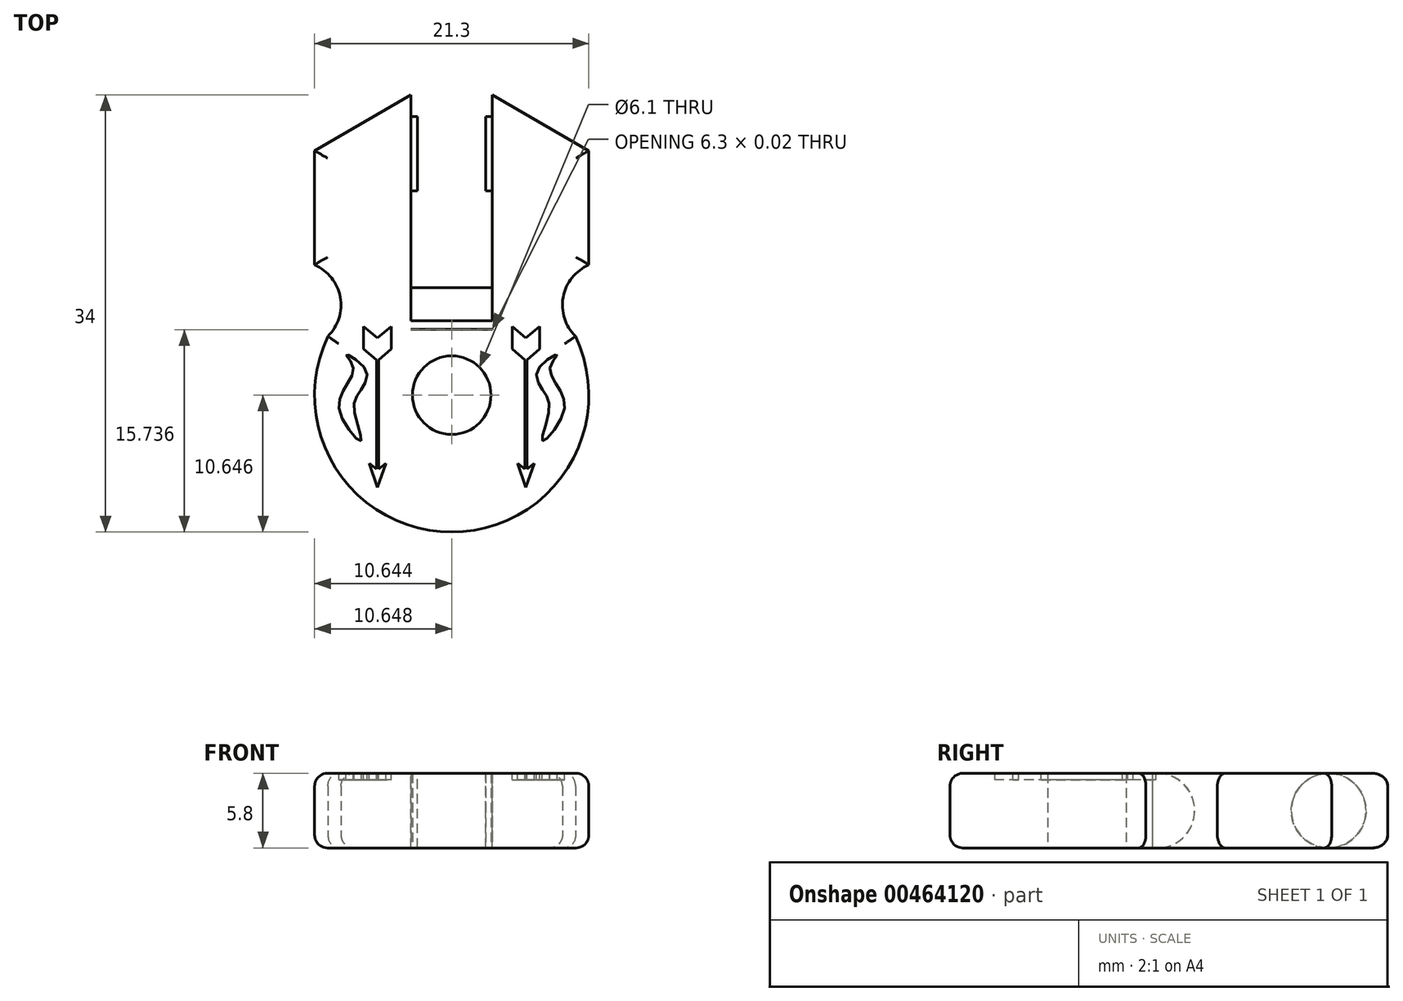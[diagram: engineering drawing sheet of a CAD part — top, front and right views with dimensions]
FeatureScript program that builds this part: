
annotation { "Feature Type Name" : "Feature", "Feature Type Description" : "" }
export const myFeature = defineFeature(function(context is Context, id is Id, definition is map)
    precondition{}
    {
        {
            var Q0;
            Q0=qCreatedBy(makeId("Top.planeOp"),FACE);
            var sketch = newSketch(context, id + "F0", { "sketchPlane" : qUnion([Q0])});
            skArc(sketch, "E0", {"start": v(-38.89, 15.42) * mm, "mid": v(-29.27, 0.2) * mm, "end": v(-19.65, 15.42) * mm});
            skLineSegment(sketch, "E1", {"start": v(-18.62, 29.85) * mm, "end": v(-26.13, 34.2) * mm});
            skLineSegment(sketch, "E2", {"start": v(-18.62, 29.85) * mm, "end": v(-18.62, 20.97) * mm});
            skPoint(sketch, "E3.start.orphan", {"position": v(-18.62, 10.85) * mm});
            skPoint(sketch, "E4.end.orphan", {"position": v(-18.32, 15.95) * mm});
            skLineSegment(sketch, "E5", {"start": v(-32.43, 34.2) * mm, "end": v(-39.92, 29.85) * mm});
            skLineSegment(sketch, "E6", {"start": v(-39.92, 29.85) * mm, "end": v(-39.92, 20.85) * mm});
            skPoint(sketch, "E7.end.orphan", {"position": v(-39.92, 34.2) * mm});
            skArc(sketch, "E8", {"start": v(-38.89, 15.42) * mm, "mid": v(-37.93, 18.47) * mm, "end": v(-39.92, 20.97) * mm});
            skPoint(sketch, "E9.orphan", {"position": v(-38.4, 16.32) * mm});
            skPoint(sketch, "E10.end.orphan", {"position": v(-29.27, -3.17) * mm});
            skArc(sketch, "E11", {"start": v(-18.62, 20.97) * mm, "mid": v(-20.61, 18.47) * mm, "end": v(-19.65, 15.42) * mm});
            skPoint(sketch, "E12.orphan", {"position": v(-20.14, 16.32) * mm});
            skLineSegment(sketch, "E13", {"start": v(-32.43, 34.2) * mm, "end": v(-32.43, 15.95) * mm});
            skLineSegment(sketch, "E14", {"start": v(-26.13, 34.2) * mm, "end": v(-26.13, 15.93) * mm});
            skPoint(sketch, "E15.end.orphan", {"position": v(-26.12, 15.93) * mm});
            skPoint(sketch, "E16.start.orphan", {"position": v(-29.27, 15.95) * mm});
            skPoint(sketch, "E17.start.orphan", {"position": v(-32.42, 15.95) * mm});
            skLineSegment(sketch, "E18", {"start": v(-26.13, 15.93) * mm, "end": v(-32.43, 15.95) * mm});
            skPoint(sketch, "E19.start.orphan", {"position": v(-26.13, 34.2) * mm});
            skPoint(sketch, "E20.orphan", {"position": v(-32.43, 34.2) * mm});
            skCircle(sketch, "E21", {"center": v(-29.27, 10.85) * mm, "radius": 3.05 * mm});
            skSolve(sketch);
        }
        {
            var Q0;
            Q0=qSketchRegion(id+"F0",true);
            extrude(context, id + "F1", {"entities" : qUnion([Q0]), "depth" : 5.8 * mm});
        }
        {
            var Q0;
            Q0=makeQuery(id+"F1.opExtrude","CAP_EDGE",EDGE,{"disambiguationData":[OSD([sQuery(id+"F0.wireOp",EDGE,"E0")])],"isStart":false});
            var Q1;
            Q1=makeQuery(id+"F1.opExtrude","CAP_EDGE",EDGE,{"disambiguationData":[OSD([sQuery(id+"F0.wireOp",EDGE,"E11")])],"isStart":false});
            var Q2;
            Q2=makeQuery(id+"F1.opExtrude","CAP_EDGE",EDGE,{"disambiguationData":[OSD([sQuery(id+"F0.wireOp",EDGE,"E2")])],"isStart":false});
            var Q3;
            Q3=makeQuery(id+"F1.opExtrude","CAP_EDGE",EDGE,{"disambiguationData":[OSD([sQuery(id+"F0.wireOp",EDGE,"E8")])],"isStart":false});
            var Q4;
            Q4=makeQuery(id+"F1.opExtrude","CAP_EDGE",EDGE,{"disambiguationData":[OSD([sQuery(id+"F0.wireOp",EDGE,"E6")])],"isStart":false});
            var Q5;
            Q5=makeQuery(id+"F1.opExtrude","CAP_EDGE",EDGE,{"disambiguationData":[OSD([sQuery(id+"F0.wireOp",EDGE,"E5")])],"isStart":false});
            var Q6;
            Q6=makeQuery(id+"F1.opExtrude","CAP_EDGE",EDGE,{"disambiguationData":[OSD([sQuery(id+"F0.wireOp",EDGE,"E1")])],"isStart":false});
            var Q7;
            Q7=makeQuery(id+"F1.opExtrude","CAP_EDGE",EDGE,{"disambiguationData":[OSD([sQuery(id+"F0.wireOp",EDGE,"E0")])],"isStart":true});
            var Q8;
            Q8=makeQuery(id+"F1.opExtrude","CAP_EDGE",EDGE,{"disambiguationData":[OSD([sQuery(id+"F0.wireOp",EDGE,"E11")])],"isStart":true});
            var Q9;
            Q9=makeQuery(id+"F1.opExtrude","CAP_EDGE",EDGE,{"disambiguationData":[OSD([sQuery(id+"F0.wireOp",EDGE,"E8")])],"isStart":true});
            var Q10;
            Q10=makeQuery(id+"F1.opExtrude","CAP_EDGE",EDGE,{"disambiguationData":[OSD([sQuery(id+"F0.wireOp",EDGE,"E6")])],"isStart":true});
            var Q11;
            Q11=makeQuery(id+"F1.opExtrude","CAP_EDGE",EDGE,{"disambiguationData":[OSD([sQuery(id+"F0.wireOp",EDGE,"E2")])],"isStart":true});
            var Q12;
            Q12=makeQuery(id+"F1.opExtrude","CAP_EDGE",EDGE,{"disambiguationData":[OSD([sQuery(id+"F0.wireOp",EDGE,"E1")])],"isStart":true});
            var Q13;
            Q13=makeQuery(id+"F1.opExtrude","CAP_EDGE",EDGE,{"disambiguationData":[OSD([sQuery(id+"F0.wireOp",EDGE,"E5")])],"isStart":true});
            fillet(context, id + "F2", {"entities" : qUnion([Q0, Q1, Q2, Q3, Q4, Q5, Q6, Q7, Q8, Q9, Q10, Q11, Q12, Q13]), "radius" : 1 * mm, "tangentPropagation" : true, "allowEdgeOverflow" : false});
        }
        {
            var Q0;
            Q0=makeQuery(id+"F1.opExtrude","SWEPT_FACE",FACE,{"disambiguationData":[OSD([sQuery(id+"F0.wireOp",EDGE,"E13")])]});
            var sketch = newSketch(context, id + "F3", { "sketchPlane" : qUnion([Q0])});
            skCircle(sketch, "E22", {"center": v(29.6, 2.9) * mm, "radius": 2.9 * mm});
            skPoint(sketch, "E23.orphan", {"position": v(34.2, 2.9) * mm});
            skArc(sketch, "E24", {"start": v(15.95, 0) * mm, "mid": v(19.2, 2.9) * mm, "end": v(15.95, 5.8) * mm});
            skSolve(sketch);
        }
        {
            var Q0;
            {var subQ0=sQuery(id+"F3.wireOp",EDGE,"E22");var subQ1=sQuery(id+"F0.wireOp",EDGE,"E13");var subQ2=makeQuery(id+"F3.imprint","INTERSECT",VERTEX,{"derivedFrom":[makeQuery(id+"F1.opExtrude","CAP_EDGE",EDGE,{"disambiguationData":[OSD([subQ1])],"isStart":true}),subQ0]});Q0=makeQuery(id+"F3.imprint","IMPRINT",FACE,{"disambiguationData":[TD([[makeQuery(id+"F3.imprint","IMPRINT",EDGE,{"disambiguationData":[TD([[subQ2,1.0]])],"derivedFrom":subQ0}),1.0]])]});}
            extrude(context, id + "F4", {"entities" : qUnion([Q0]), "operationType" : NewBodyOperationType.ADD, "depth" : .5 * mm});
        }
        {
            var Q0;
            {var subQ1=sQuery(id+"F0.wireOp",EDGE,"E13");var subQ6=makeQuery(id+"F1.opExtrude","SWEPT_EDGE",EDGE,{"disambiguationData":[OSD([subQ1,sQuery(id+"F0.wireOp",EDGE,"E18")])]});Q0=makeQuery(id+"F3.imprint","IMPRINT",FACE,{"disambiguationData":[TD([[makeQuery(id+"F3.imprint","IMPRINT",EDGE,{"derivedFrom":subQ6}),1.0]])]});}
            extrude(context, id + "F5", {"entities" : qUnion([Q0]), "operationType" : NewBodyOperationType.ADD, "depth" : 8.2 * mm});
        }
        {
            var Q0;
            Q0=makeQuery(id+"F1.opExtrude","SWEPT_FACE",FACE,{"disambiguationData":[OSD([sQuery(id+"F0.wireOp",EDGE,"E14")])]});
            var sketch = newSketch(context, id + "F6", { "sketchPlane" : qUnion([Q0])});
            skCircle(sketch, "E25", {"center": v(-29.6, 2.9) * mm, "radius": 2.9 * mm});
            skPoint(sketch, "E26.orphan", {"position": v(-34.2, 2.9) * mm});
            skSolve(sketch);
        }
        {
            var Q0;
            Q0=qSketchRegion(id+"F6",true);
            extrude(context, id + "F7", {"entities" : qUnion([Q0]), "operationType" : NewBodyOperationType.ADD, "depth" : .5 * mm});
        }
        {
            var Q0;
            Q0=makeQuery(id+"F1.opExtrude","CAP_FACE",FACE,{"disambiguationData":[OSD([sQuery(id+"F0.wireOp",EDGE,"E0"),sQuery(id+"F0.wireOp",EDGE,"E1"),sQuery(id+"F0.wireOp",EDGE,"E2"),sQuery(id+"F0.wireOp",EDGE,"E5"),sQuery(id+"F0.wireOp",EDGE,"E6"),sQuery(id+"F0.wireOp",EDGE,"E8"),sQuery(id+"F0.wireOp",EDGE,"E11"),sQuery(id+"F0.wireOp",EDGE,"E13"),sQuery(id+"F0.wireOp",EDGE,"E14"),sQuery(id+"F0.wireOp",EDGE,"E18"),sQuery(id+"F0.wireOp",EDGE,"E21")])],"isStart":false});
            var sketch = newSketch(context, id + "F8", { "sketchPlane" : qUnion([Q0])});
            skLineSegment(sketch, "E27", {"start": v(-35.04, 15.28) * mm, "end": v(-36.11, 16.18) * mm});
            skLineSegment(sketch, "E28", {"start": v(-36.11, 16.18) * mm, "end": v(-36.11, 14.43) * mm});
            skLineSegment(sketch, "E29", {"start": v(-36.11, 14.43) * mm, "end": v(-35.11, 13.6) * mm});
            skLineSegment(sketch, "E30", {"start": v(-35.11, 13.6) * mm, "end": v(-35.11, 5.1) * mm});
            skLineSegment(sketch, "E31", {"start": v(-35.11, 5.1) * mm, "end": v(-35.7, 5.54) * mm});
            skLineSegment(sketch, "E32", {"start": v(-35.7, 5.54) * mm, "end": v(-35.04, 3.69) * mm});
            skLineSegment(sketch, "E33.MirrorCS", {"start": v(-34.38, 5.54) * mm, "end": v(-35.04, 3.69) * mm});
            skLineSegment(sketch, "E34.MirrorCS", {"start": v(-34.96, 5.1) * mm, "end": v(-34.38, 5.54) * mm});
            skLineSegment(sketch, "E35.MirrorCS", {"start": v(-34.96, 13.6) * mm, "end": v(-34.96, 5.1) * mm});
            skLineSegment(sketch, "E36.MirrorCS", {"start": v(-33.97, 14.43) * mm, "end": v(-34.96, 13.6) * mm});
            skLineSegment(sketch, "E37.MirrorCS", {"start": v(-33.97, 16.18) * mm, "end": v(-33.97, 14.43) * mm});
            skLineSegment(sketch, "E38.MirrorCS", {"start": v(-35.04, 15.28) * mm, "end": v(-33.97, 16.18) * mm});
            skLineSegment(sketch, "E39.MirrorCS", {"start": v(-24.16, 5.54) * mm, "end": v(-23.5, 3.69) * mm});
            skLineSegment(sketch, "E40.MirrorCS", {"start": v(-22.85, 5.54) * mm, "end": v(-23.5, 3.69) * mm});
            skLineSegment(sketch, "E41.MirrorCS", {"start": v(-23.43, 5.1) * mm, "end": v(-22.85, 5.54) * mm});
            skLineSegment(sketch, "E42.MirrorCS", {"start": v(-23.58, 5.1) * mm, "end": v(-24.16, 5.54) * mm});
            skLineSegment(sketch, "E43.MirrorCS", {"start": v(-23.58, 13.6) * mm, "end": v(-23.58, 5.1) * mm});
            skLineSegment(sketch, "E44.MirrorCS", {"start": v(-23.43, 13.6) * mm, "end": v(-23.43, 5.1) * mm});
            skLineSegment(sketch, "E45.MirrorCS", {"start": v(-24.58, 14.43) * mm, "end": v(-23.58, 13.6) * mm});
            skLineSegment(sketch, "E46.MirrorCS", {"start": v(-22.43, 14.43) * mm, "end": v(-23.43, 13.6) * mm});
            skLineSegment(sketch, "E47.MirrorCS", {"start": v(-22.43, 16.18) * mm, "end": v(-22.43, 14.43) * mm});
            skLineSegment(sketch, "E48.MirrorCS", {"start": v(-23.5, 15.28) * mm, "end": v(-22.43, 16.18) * mm});
            skLineSegment(sketch, "E49.MirrorCS", {"start": v(-23.5, 15.28) * mm, "end": v(-24.58, 16.18) * mm});
            skLineSegment(sketch, "E50.MirrorCS", {"start": v(-24.58, 16.18) * mm, "end": v(-24.58, 14.43) * mm});
            skPoint(sketch, "E51.endSnap0", {"position": v(-37.4, 6.72) * mm});
            skFitSpline(sketch, "E52", {"points": [v(-36.32, 7.3) * mm, v(-37.9, 9.33) * mm, v(-37.56, 11.44) * mm, v(-36.94, 13.12) * mm, v(-37.47, 14) * mm, v(-35.97, 12.86) * mm, v(-36.32, 11.27) * mm, v(-36.85, 9.77) * mm, v(-36.32, 7.3) * mm]});
            skFitSpline(sketch, "E53.MirrorC", {"points": [v(-22.22, 7.3) * mm, v(-20.63, 9.33) * mm, v(-20.99, 11.44) * mm, v(-21.6, 13.12) * mm, v(-21.08, 14) * mm, v(-22.58, 12.86) * mm, v(-22.22, 11.27) * mm, v(-21.7, 9.77) * mm, v(-22.22, 7.3) * mm]});
            skSolve(sketch);
        }
        {
            var Q0;
            Q0=qSketchRegion(id+"F8",true);
            extrude(context, id + "F9", {"entities" : qUnion([Q0]), "operationType" : NewBodyOperationType.REMOVE, "oppositeDirection" : true, "depth" : .5 * mm});
        }
    });
